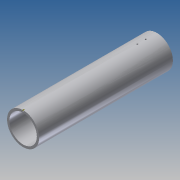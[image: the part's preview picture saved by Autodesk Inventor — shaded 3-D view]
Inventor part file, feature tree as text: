
AUTODESK INVENTOR PART (.ipt)
format: ipt  version: 2014 SP1 (Build 180222100, 222)  size: 121,856 bytes
history: native  units: in
note: dims shown in document units (in); Inventor stores cm internally (conversion verified against a paired STEP export)
features: sketch x5, extrude x2, plane x2, hole x1
ambient origin geometry x8: Origin, YZ Plane, XZ Plane, XY Plane, X Axis, Y Axis, Z Axis, Center Point
bodies: Solid1 (feature_tree)
feature tree (10):
  extrude  "Extrusion1"  Depth=0.203in
  sketch  "Sketch2"  dims[d3=12.0in d4=0.0in d25=1.0in]
  plane  "Work Plane1"
  hole  "Hole3"  [1 undecoded]
  sketch  "Sketch6"  dims[d27=0.125in d28=0.75in d29=0.375in d30=0.25in d31=0.5635in d32=1.0in d33=0.8108in d34=0.1in]
  plane  "Work Plane2"
  extrude  "angleNotch"  Depth=0.1in
  sketch  "Sketch1"  dims[d0=2.875in d2=0.203in]
  sketch  "Sketch5"  dims[d26=0.75in]
  sketch  "Sketch8"  dims[d35=0.1in d36=0.1in d37=0.0in]
note: 1 required parameter value undecoded (feature->parameter linkage not recoverable at this tier; creation-order binding heuristic only, values carry confidence <= 0.55)
